# Revit family: QF_ADVENTYS_ADV2026-B_KTI1_360x360_6000_W_Géné_déporté
name_source: partatom
category: Attrezzature speciali
units: mm (PartAtom-declared; Revit-internal decimal feet)

## family parameters
Condiviso = No
Host = Superficie
Punto di calcolo locali = No
Quota connettore circolare = Usa diametro
Taglio con vuoti quando caricato = No
Tipo di parte = Normale

## types (1)
- ADV2026-B
    Controller_Height = 120 mm  [stored 0.393701 ft]
    Controller_Width = 250 mm  [stored 0.82021 ft]
    Cycle = 50 Hz
    Depth = 360 mm  [stored 1.1811 ft]
    Depth Actual = 360 mm  [stored 1.1811 ft]
    Height = 63 mm  [stored 0.206693 ft]
    Height Actual = 75 mm
    Item Number = ADV2026-B
    Length Actual = 360 mm  [stored 1.1811 ft]
    Modello = KTI1 360x360 6000 W Géné déporté
    Phase = 3
    Produttore = ADVENTYS
    Prospetto di default = 1219.2 mm  [stored 4 ft]
    URL = https://adventys.com
    Volts = 380 V
    Watts = 6000 W
    Weight = 10
    Width = 360 mm  [stored 1.1811 ft]

note: [stored X ft] marks values corroborated as IEEE doubles in the binary element streams (Revit-internal decimal feet)

## geometry (parser evidence)
native form markers: Sweep x2
no freeform markers — native parametric forms only
